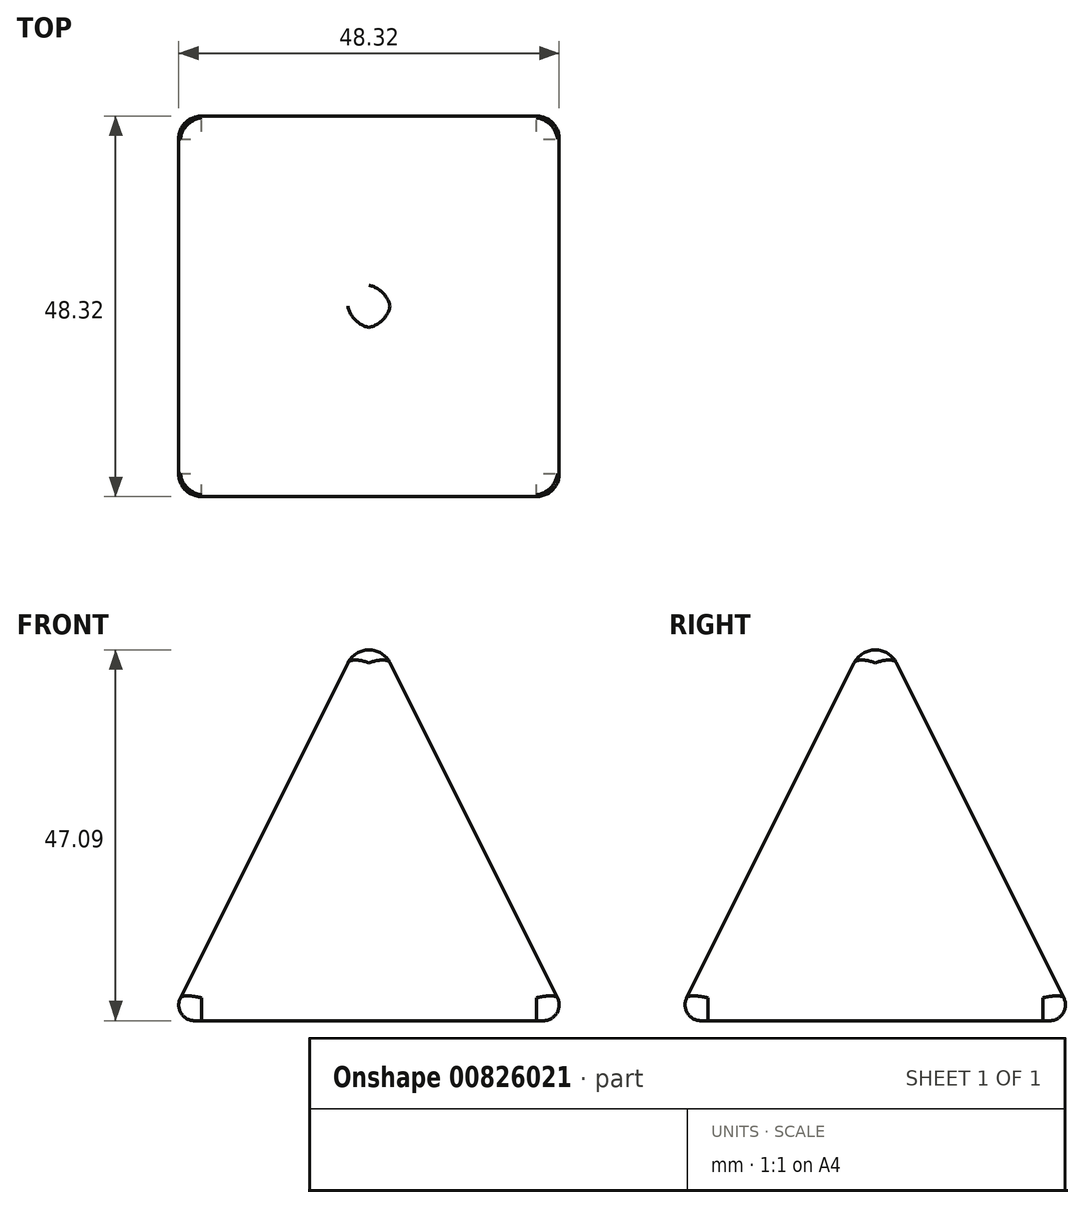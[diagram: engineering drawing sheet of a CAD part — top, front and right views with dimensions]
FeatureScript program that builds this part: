
annotation { "Feature Type Name" : "Feature", "Feature Type Description" : "" }
export const myFeature = defineFeature(function(context is Context, id is Id, definition is map)
    precondition{}
    {
        {
            var Q0;
            Q0=qCreatedBy(makeId("Top.planeOp"),FACE);
            var sketch = newSketch(context, id + "F0", { "sketchPlane" : qUnion([Q0])});
            skPoint(sketch, "E0", {"position": v(-25.4, -25.4) * mm});
            skLineSegment(sketch, "E1", {"start": v(0, -25.4) * mm, "end": v(-25.4, -25.4) * mm});
            skLineSegment(sketch, "E2", {"start": v(-25.4, -25.4) * mm, "end": v(-25.4, 0) * mm});
            skLineSegment(sketch, "E3.MirrorCS", {"start": v(-25.4, 25.4) * mm, "end": v(-25.4, 0) * mm});
            skLineSegment(sketch, "E4.MirrorCS", {"start": v(0, 25.4) * mm, "end": v(-25.4, 25.4) * mm});
            skLineSegment(sketch, "E5.MirrorCS", {"start": v(0, 25.4) * mm, "end": v(25.4, 25.4) * mm});
            skLineSegment(sketch, "E6.MirrorCS", {"start": v(25.4, 25.4) * mm, "end": v(25.4, 0) * mm});
            skLineSegment(sketch, "E7.MirrorCS", {"start": v(25.4, -25.4) * mm, "end": v(25.4, 0) * mm});
            skLineSegment(sketch, "E8.MirrorCS", {"start": v(0, -25.4) * mm, "end": v(25.4, -25.4) * mm});
            skSolve(sketch);
        }
        {
            var Q0;
            Q0=qCreatedBy(makeId("Top.planeOp"),FACE);
            cPlane(context, id + "F1", {"entities" : qUnion([Q0]), "cplaneType" : CPlaneType.OFFSET, "offset" : 50.8 * mm, "width" : 152.4 * mm, "height" : 152.4 * mm});
        }
        {
            var Q0;
            Q0=qCreatedBy(id+"F1.planeOp",FACE);
            var sketch = newSketch(context, id + "F2", { "sketchPlane" : qUnion([Q0])});
            skPoint(sketch, "E9", {"position": v(0, 0) * mm});
            skSolve(sketch);
        }
        {
            var Q0;
            Q0=sQuery(id+"F2.wireOp",VERTEX,"E9");
            var Q1;
            Q1=makeQuery(id+"F0.imprint","IMPRINT",FACE,{"disambiguationData":[TD([[makeQuery(id+"F0.imprint","IMPRINT",EDGE,{"derivedFrom":sQuery(id+"F0.wireOp",EDGE,"E1")}),-1.0]])]});
            loft(context, id + "F3", {"sheetProfilesArray" : [{ "sheetProfileEntities" : qUnion([Q0]) }, { "sheetProfileEntities" : qUnion([Q1]) }]});
        }
        {
            var Q0;
            Q0=makeQuery(id+"F3.opLoft","SWEPT_EDGE",EDGE,{"disambiguationData":[OSD([sQuery(id+"F0.wireOp",EDGE,"E1"),sQuery(id+"F0.wireOp",EDGE,"E2"),sQuery(id+"F2.wireOp",VERTEX,"E9")])]});
            var Q1;
            Q1=makeQuery(id+"F3.opLoft","SWEPT_EDGE",EDGE,{"disambiguationData":[OSD([sQuery(id+"F0.wireOp",EDGE,"E7.MirrorCS"),sQuery(id+"F0.wireOp",EDGE,"E8.MirrorCS"),sQuery(id+"F2.wireOp",VERTEX,"E9")])]});
            var Q2;
            Q2=makeQuery(id+"F3.opLoft","SWEPT_EDGE",EDGE,{"disambiguationData":[OSD([sQuery(id+"F0.wireOp",EDGE,"E3.MirrorCS"),sQuery(id+"F0.wireOp",EDGE,"E4.MirrorCS"),sQuery(id+"F2.wireOp",VERTEX,"E9")])]});
            var Q3;
            Q3=makeQuery(id+"F3.opLoft","SWEPT_EDGE",EDGE,{"disambiguationData":[OSD([sQuery(id+"F0.wireOp",EDGE,"E5.MirrorCS"),sQuery(id+"F0.wireOp",EDGE,"E6.MirrorCS"),sQuery(id+"F2.wireOp",VERTEX,"E9")])]});
            fillet(context, id + "F4", {"entities" : qUnion([Q0, Q1, Q2, Q3]), "radius" : 3 * mm, "tangentPropagation" : true, "allowEdgeOverflow" : false});
        }
        {
            var Q0;
            Q0=makeQuery(id+"F3.opLoft","MID_CAP_EDGE",EDGE,{"disambiguationData":[OSD([sQuery(id+"F0.wireOp",EDGE,"E1"),sQuery(id+"F0.wireOp",EDGE,"E7.MirrorCS"),sQuery(id+"F0.wireOp",EDGE,"E8.MirrorCS")])],"capPos":1.0});
            fillet(context, id + "F5", {"entities" : qUnion([Q0]), "radius" : 2 * mm, "tangentPropagation" : true, "allowEdgeOverflow" : false});
        }
    });
